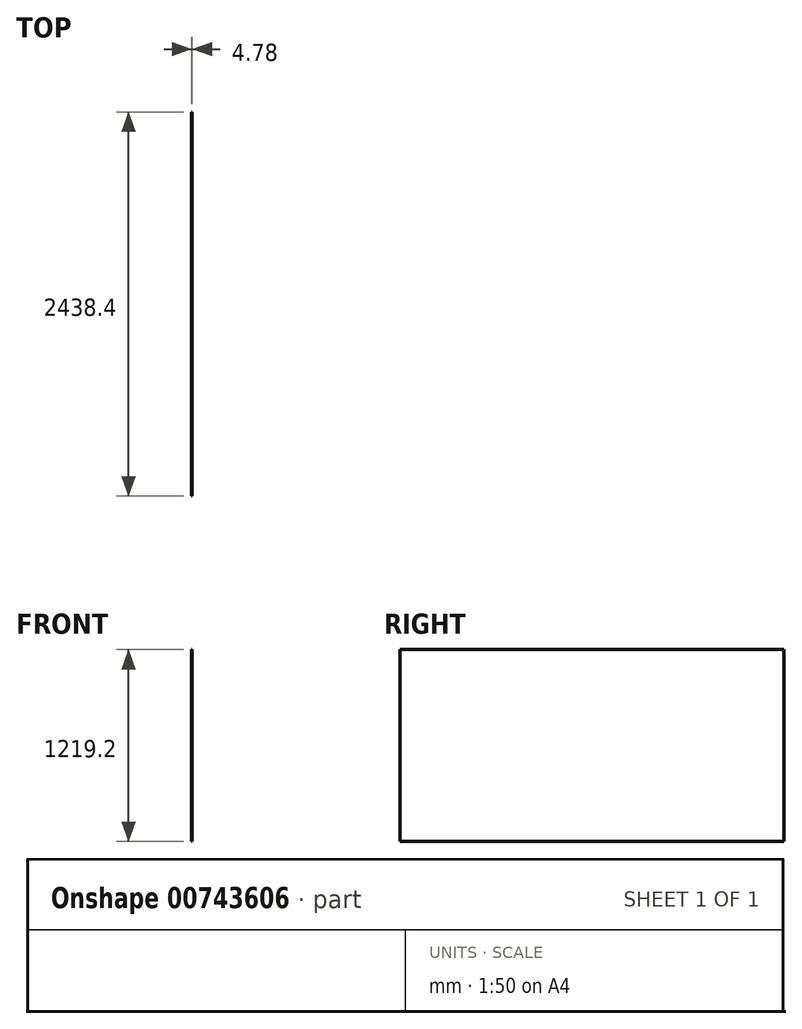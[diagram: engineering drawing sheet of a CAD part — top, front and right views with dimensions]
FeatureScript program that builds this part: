
annotation { "Feature Type Name" : "Feature", "Feature Type Description" : "" }
export const myFeature = defineFeature(function(context is Context, id is Id, definition is map)
    precondition{}
    {
        {
            var Q0;
            Q0=qCreatedBy(makeId("Right.planeOp"),FACE);
            var sketch = newSketch(context, id + "F0", { "sketchPlane" : qUnion([Q0])});
            skPoint(sketch, "E0.middle", {"position": v(0, 0) * mm});
            skLineSegment(sketch, "E1.bottom", {"start": v(-1219.2, -609.6) * mm, "end": v(1219.2, -609.6) * mm});
            skLineSegment(sketch, "E1.top", {"start": v(-1219.2, 609.6) * mm, "end": v(1219.2, 609.6) * mm});
            skLineSegment(sketch, "E1.left", {"start": v(-1219.2, -609.6) * mm, "end": v(-1219.2, 609.6) * mm});
            skLineSegment(sketch, "E1.right", {"start": v(1219.2, -609.6) * mm, "end": v(1219.2, 609.6) * mm});
            skSolve(sketch);
        }
        {
            var Q0;
            Q0=makeQuery(id+"F0.imprint","IMPRINT",FACE,{"disambiguationData":[TD([[makeQuery(id+"F0.imprint","IMPRINT",EDGE,{"derivedFrom":sQuery(id+"F0.wireOp",EDGE,"E1.bottom")}),1.0]])]});
            extrude(context, id + "F1", {"entities" : qUnion([Q0]), "depth" : 4.78 * mm, "offsetDistance" : 25.4 * mm});
        }
    });
